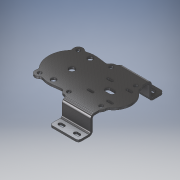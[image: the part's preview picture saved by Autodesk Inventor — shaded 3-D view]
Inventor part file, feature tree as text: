
AUTODESK INVENTOR PART (.ipt)
format: ipt  version: 2017 (Build 210142000, 142)  size: 431,104 bytes
history: native  units: mm
features: extrude x6, sketch x6, fillet x4, mirror x2, other x1, plane x1
ambient origin geometry x8: Origin, YZ Plane, XZ Plane, XY Plane, X Axis, Y Axis, Z Axis, Center Point
bodies: Body1 (feature_tree)
feature tree (20):
  other  "Sólido1"
  extrude  "Extrusión1"  Depth=88.9mm
  plane  "Plano de trabajo1"
  extrude  "Extrusión3"  Depth=22.225mm
  mirror  "Simetría1"
  extrude  "Extrusión2"  Depth=22.225mm
  fillet  "Empalme6"  Radius=22.225mm
  extrude  "Extrusión5"  TaperAngle=0.0deg  [1 undecoded]
  extrude  "Extrusión6"  Depth=5.0mm TaperAngle=0.0deg
  fillet  "Empalme7"  Radius=9.525mm
  fillet  "Empalme8"  Radius=9.525mm
  fillet  "Empalme9"  Radius=9.525mm
  extrude  "Extrusión8"  Depth=8.73125mm
  mirror  "Simetría3"
  sketch  "Boceto1"  dims[d0=114.3mm d1=88.9mm]
  sketch  "Boceto2"  dims[d2=203.2mm d3=22.225mm]
  sketch  "Boceto3"  dims[d4=22.225mm d7=22.225mm d8=22.225mm]
  sketch  "Boceto5"  dims[d11=22.225mm d13=0.0mm]
  sketch  "Boceto6"  dims[d14=22.225mm d16=5.0mm d17=0.0mm d18=9.525mm d19=9.525mm d20=9.525mm]
  sketch  "Boceto8"  dims[d21=9.525mm d22=9.525mm d23=9.525mm d24=25.4mm d25=0.0mm d27=50.8mm d33=69.85mm d34=0.0mm d35=31.75mm d36=31.75mm d37=44.45mm d38=44.45mm d39=12.7mm d40=12.7mm d57=6.35mm d58=14.2875mm d59=45.0mm d60=45.0mm d61=12.7mm d62=12.7mm d63=25.4mm d64=0.0mm d65=12.7mm d66=0.0mm d67=93.4212mm d68=12.7mm d69=12.7mm d70=5.159375mm d71=5.159375mm d72=47.5mm d73=47.5mm d74=23.75mm d75=23.75mm d76=5.55625mm d77=5.55625mm d78=5.159375mm d79=5.159375mm d80=0.0mm d81=5.55625mm d82=5.55625mm d83=5.159375mm d84=5.159375mm d85=0.0mm d86=0.0mm d87=5.55625mm d88=5.55625mm d89=5.159375mm d90=5.159375mm d91=0.0mm d92=5.55625mm d93=5.55625mm d94=5.159375mm d95=5.159375mm d96=0.0mm d97=25.4mm d98=0.0mm d123=69.85mm d124=44.45mm d125=104.775mm d126=5.0mm d127=5.0mm d128=4.445mm d129=8.89mm d130=6.35mm d131=8.73125mm d132=15.875mm d133=8.73125mm d134=8.73125mm d135=3.373438mm d136=12.7mm d137=8.73125mm d138=8.73125mm d139=8.73125mm d140=12.7mm d141=15.875mm d142=25.4mm d143=0.0mm]
note: 1 required parameter value undecoded (feature->parameter linkage not recoverable at this tier; creation-order binding heuristic only, values carry confidence <= 0.55)
